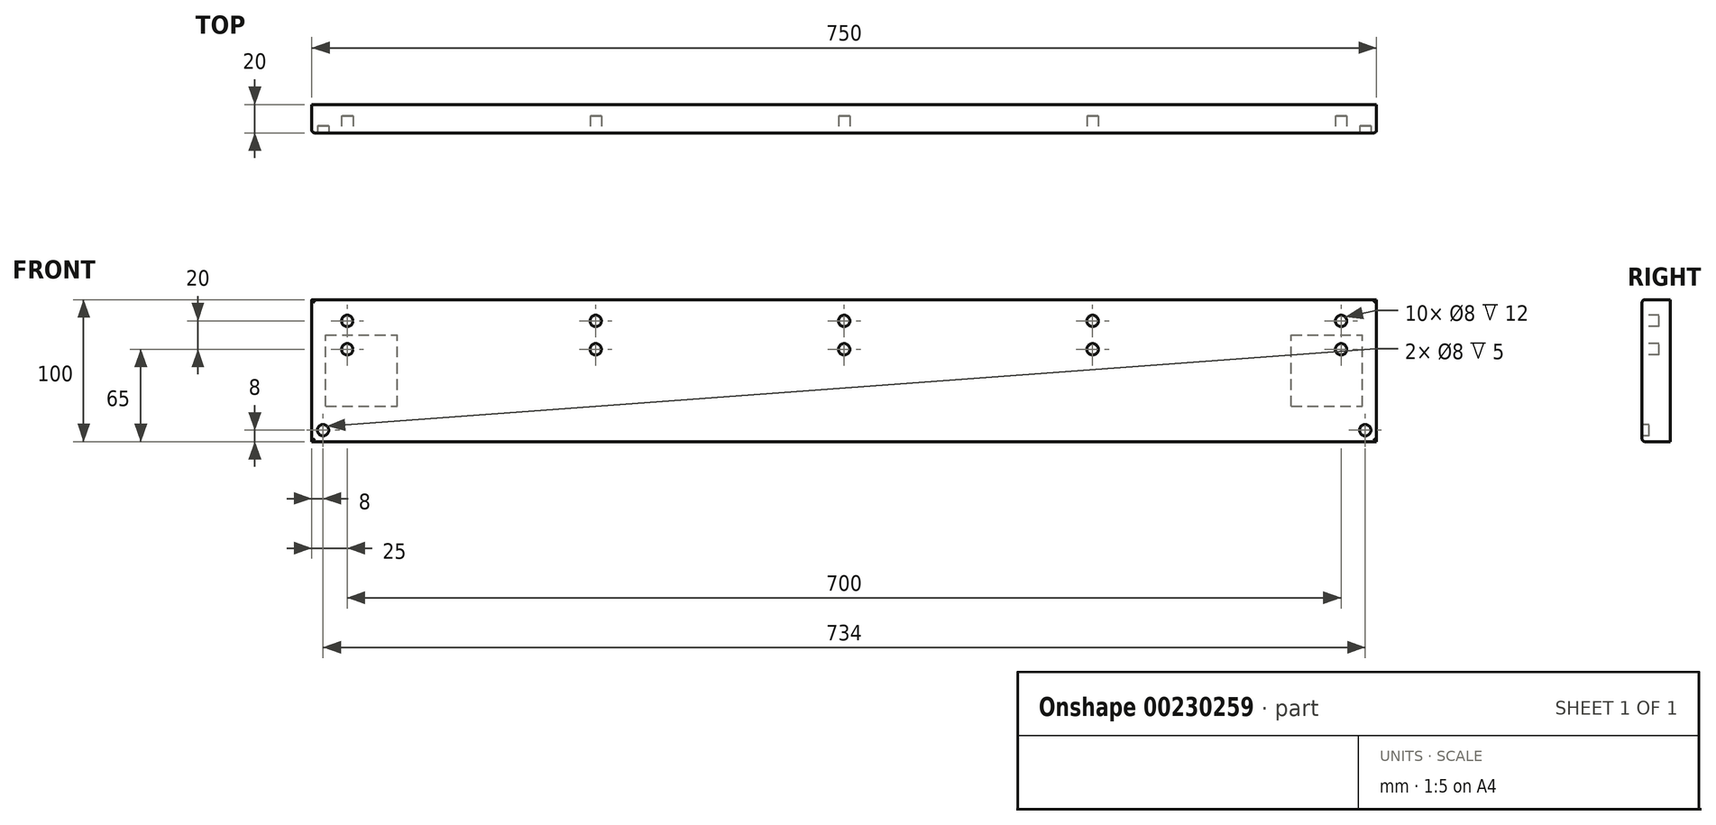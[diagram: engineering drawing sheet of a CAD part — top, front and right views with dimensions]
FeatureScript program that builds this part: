
annotation { "Feature Type Name" : "Feature", "Feature Type Description" : "" }
export const myFeature = defineFeature(function(context is Context, id is Id, definition is map)
    precondition{}
    {
        {
            var Q0;
            Q0=qCreatedBy(makeId("Front.planeOp"),FACE);
            var sketch = newSketch(context, id + "F0", { "sketchPlane" : qUnion([Q0])});
            skLineSegment(sketch, "E0.bottom", {"start": v(375, -50) * mm, "end": v(-375, -50) * mm});
            skLineSegment(sketch, "E0.top", {"start": v(375, 50) * mm, "end": v(-375, 50) * mm});
            skLineSegment(sketch, "E0.left", {"start": v(375, -50) * mm, "end": v(375, 50) * mm});
            skLineSegment(sketch, "E0.right", {"start": v(-375, -50) * mm, "end": v(-375, 50) * mm});
            skPoint(sketch, "E0.middle", {"position": v(0, 0) * mm});
            skSolve(sketch);
        }
        {
            var Q0;
            Q0=makeQuery(id+"F0.imprint","IMPRINT",FACE,{"disambiguationData":[TD([[makeQuery(id+"F0.imprint","IMPRINT",EDGE,{"derivedFrom":sQuery(id+"F0.wireOp",EDGE,"E0.bottom")}),-1.0]])]});
            extrude(context, id + "F1", {"entities" : qUnion([Q0]), "depth" : 20 * mm});
        }
        {
            var Q0;
            Q0=makeQuery(id+"F1.opExtrude","CAP_FACE",FACE,{"disambiguationData":[OSD([sQuery(id+"F0.wireOp",EDGE,"E0.bottom"),sQuery(id+"F0.wireOp",EDGE,"E0.top"),sQuery(id+"F0.wireOp",EDGE,"E0.left"),sQuery(id+"F0.wireOp",EDGE,"E0.right")])],"isStart":false});
            fillet(context, id + "F2", {"entities" : qUnion([Q0]), "radius" : 2 * mm, "tangentPropagation" : true, "allowEdgeOverflow" : false});
        }
        {
            var Q0;
            Q0=makeQuery(id+"F1.opExtrude","CAP_FACE",FACE,{"disambiguationData":[OSD([sQuery(id+"F0.wireOp",EDGE,"E0.bottom"),sQuery(id+"F0.wireOp",EDGE,"E0.top"),sQuery(id+"F0.wireOp",EDGE,"E0.left"),sQuery(id+"F0.wireOp",EDGE,"E0.right")])],"isStart":false});
            var sketch = newSketch(context, id + "F3", { "sketchPlane" : qUnion([Q0])});
            skCircle(sketch, "E1", {"center": v(-350, 35) * mm, "radius": 4 * mm});
            skCircle(sketch, "E2", {"center": v(-175, 35) * mm, "radius": 4 * mm});
            skCircle(sketch, "E3", {"center": v(0, 35) * mm, "radius": 4 * mm});
            skCircle(sketch, "E4", {"center": v(-350, 15) * mm, "radius": 4 * mm});
            skCircle(sketch, "E5", {"center": v(-175, 15) * mm, "radius": 4 * mm});
            skCircle(sketch, "E6", {"center": v(0, 15) * mm, "radius": 4 * mm});
            skCircle(sketch, "E7", {"center": v(175, 35) * mm, "radius": 4 * mm});
            skCircle(sketch, "E8", {"center": v(175, 15) * mm, "radius": 4 * mm});
            skCircle(sketch, "E9", {"center": v(350, 35) * mm, "radius": 4 * mm});
            skCircle(sketch, "E10", {"center": v(350, 15) * mm, "radius": 4 * mm});
            skSolve(sketch);
        }
        {
            var Q0;
            Q0=makeQuery(id+"F3.imprint","IMPRINT",FACE,{"disambiguationData":[TD([[makeQuery(id+"F3.imprint","IMPRINT",EDGE,{"derivedFrom":sQuery(id+"F3.wireOp",EDGE,"E1")}),1.0]])]});
            var Q1;
            Q1=makeQuery(id+"F3.imprint","IMPRINT",FACE,{"disambiguationData":[TD([[makeQuery(id+"F3.imprint","IMPRINT",EDGE,{"derivedFrom":sQuery(id+"F3.wireOp",EDGE,"E4")}),1.0]])]});
            var Q2;
            Q2=makeQuery(id+"F3.imprint","IMPRINT",FACE,{"disambiguationData":[TD([[makeQuery(id+"F3.imprint","IMPRINT",EDGE,{"derivedFrom":sQuery(id+"F3.wireOp",EDGE,"E5")}),1.0]])]});
            var Q3;
            Q3=makeQuery(id+"F3.imprint","IMPRINT",FACE,{"disambiguationData":[TD([[makeQuery(id+"F3.imprint","IMPRINT",EDGE,{"derivedFrom":sQuery(id+"F3.wireOp",EDGE,"E2")}),1.0]])]});
            var Q4;
            Q4=makeQuery(id+"F3.imprint","IMPRINT",FACE,{"disambiguationData":[TD([[makeQuery(id+"F3.imprint","IMPRINT",EDGE,{"derivedFrom":sQuery(id+"F3.wireOp",EDGE,"E3")}),1.0]])]});
            var Q5;
            Q5=makeQuery(id+"F3.imprint","IMPRINT",FACE,{"disambiguationData":[TD([[makeQuery(id+"F3.imprint","IMPRINT",EDGE,{"derivedFrom":sQuery(id+"F3.wireOp",EDGE,"E6")}),1.0]])]});
            var Q6;
            Q6=makeQuery(id+"F3.imprint","IMPRINT",FACE,{"disambiguationData":[TD([[makeQuery(id+"F3.imprint","IMPRINT",EDGE,{"derivedFrom":sQuery(id+"F3.wireOp",EDGE,"E7")}),1.0]])]});
            var Q7;
            Q7=makeQuery(id+"F3.imprint","IMPRINT",FACE,{"disambiguationData":[TD([[makeQuery(id+"F3.imprint","IMPRINT",EDGE,{"derivedFrom":sQuery(id+"F3.wireOp",EDGE,"E8")}),1.0]])]});
            var Q8;
            Q8=makeQuery(id+"F3.imprint","IMPRINT",FACE,{"disambiguationData":[TD([[makeQuery(id+"F3.imprint","IMPRINT",EDGE,{"derivedFrom":sQuery(id+"F3.wireOp",EDGE,"E10")}),1.0]])]});
            var Q9;
            Q9=makeQuery(id+"F3.imprint","IMPRINT",FACE,{"disambiguationData":[TD([[makeQuery(id+"F3.imprint","IMPRINT",EDGE,{"derivedFrom":sQuery(id+"F3.wireOp",EDGE,"E9")}),1.0]])]});
            extrude(context, id + "F4", {"entities" : qUnion([Q0, Q1, Q2, Q3, Q4, Q5, Q6, Q7, Q8, Q9]), "operationType" : NewBodyOperationType.REMOVE, "oppositeDirection" : true, "depth" : 12 * mm});
        }
        {
            var Q0;
            Q0=makeQuery(id+"F1.opExtrude","CAP_FACE",FACE,{"disambiguationData":[OSD([sQuery(id+"F0.wireOp",EDGE,"E0.bottom"),sQuery(id+"F0.wireOp",EDGE,"E0.top"),sQuery(id+"F0.wireOp",EDGE,"E0.left"),sQuery(id+"F0.wireOp",EDGE,"E0.right")])],"isStart":false});
            var sketch = newSketch(context, id + "F5", { "sketchPlane" : qUnion([Q0])});
            skCircle(sketch, "E11", {"center": v(-367, -42) * mm, "radius": 4 * mm});
            skCircle(sketch, "E12", {"center": v(367, -42) * mm, "radius": 4 * mm});
            skSolve(sketch);
        }
        {
            var Q0;
            Q0=makeQuery(id+"F5.imprint","IMPRINT",FACE,{"disambiguationData":[TD([[makeQuery(id+"F5.imprint","IMPRINT",EDGE,{"derivedFrom":sQuery(id+"F5.wireOp",EDGE,"E11")}),1.0]])]});
            var Q1;
            Q1=makeQuery(id+"F5.imprint","IMPRINT",FACE,{"disambiguationData":[TD([[makeQuery(id+"F5.imprint","IMPRINT",EDGE,{"derivedFrom":sQuery(id+"F5.wireOp",EDGE,"E12")}),1.0]])]});
            extrude(context, id + "F6", {"entities" : qUnion([Q0, Q1]), "operationType" : NewBodyOperationType.REMOVE, "oppositeDirection" : true, "depth" : 5 * mm});
        }
        {
            var Q0;
            Q0=makeQuery(id+"F1.opExtrude","CAP_FACE",FACE,{"disambiguationData":[OSD([sQuery(id+"F0.wireOp",EDGE,"E0.bottom"),sQuery(id+"F0.wireOp",EDGE,"E0.top"),sQuery(id+"F0.wireOp",EDGE,"E0.left"),sQuery(id+"F0.wireOp",EDGE,"E0.right")])],"isStart":true});
            var sketch = newSketch(context, id + "F7", { "sketchPlane" : qUnion([Q0])});
            skLineSegment(sketch, "E13.bottom", {"start": v(-314.9, -25.1) * mm, "end": v(-365.1, -25.1) * mm});
            skLineSegment(sketch, "E13.top", {"start": v(-314.9, 25.1) * mm, "end": v(-365.1, 25.1) * mm});
            skLineSegment(sketch, "E13.left", {"start": v(-314.9, -25.1) * mm, "end": v(-314.9, 25.1) * mm});
            skLineSegment(sketch, "E13.right", {"start": v(-365.1, -25.1) * mm, "end": v(-365.1, 25.1) * mm});
            skPoint(sketch, "E13.middle", {"position": v(-340, 0) * mm});
            skLineSegment(sketch, "E14.bottom", {"start": v(365.1, -25.1) * mm, "end": v(314.9, -25.1) * mm});
            skLineSegment(sketch, "E14.top", {"start": v(365.1, 25.1) * mm, "end": v(314.9, 25.1) * mm});
            skLineSegment(sketch, "E14.left", {"start": v(365.1, -25.1) * mm, "end": v(365.1, 25.1) * mm});
            skLineSegment(sketch, "E14.right", {"start": v(314.9, -25.1) * mm, "end": v(314.9, 25.1) * mm});
            skPoint(sketch, "E14.middle", {"position": v(340, 0) * mm});
            skSolve(sketch);
        }
        {
            var Q0;
            Q0=makeQuery(id+"F7.imprint","IMPRINT",FACE,{"disambiguationData":[TD([[makeQuery(id+"F7.imprint","IMPRINT",EDGE,{"derivedFrom":sQuery(id+"F7.wireOp",EDGE,"E13.bottom")}),-1.0]])]});
            var Q1;
            Q1=makeQuery(id+"F7.imprint","IMPRINT",FACE,{"disambiguationData":[TD([[makeQuery(id+"F7.imprint","IMPRINT",EDGE,{"derivedFrom":sQuery(id+"F7.wireOp",EDGE,"E14.bottom")}),-1.0]])]});
            extrude(context, id + "F8", {"entities" : qUnion([Q0, Q1]), "operationType" : NewBodyOperationType.REMOVE, "oppositeDirection" : true, "depth" : 0.3 * mm});
        }
    });
